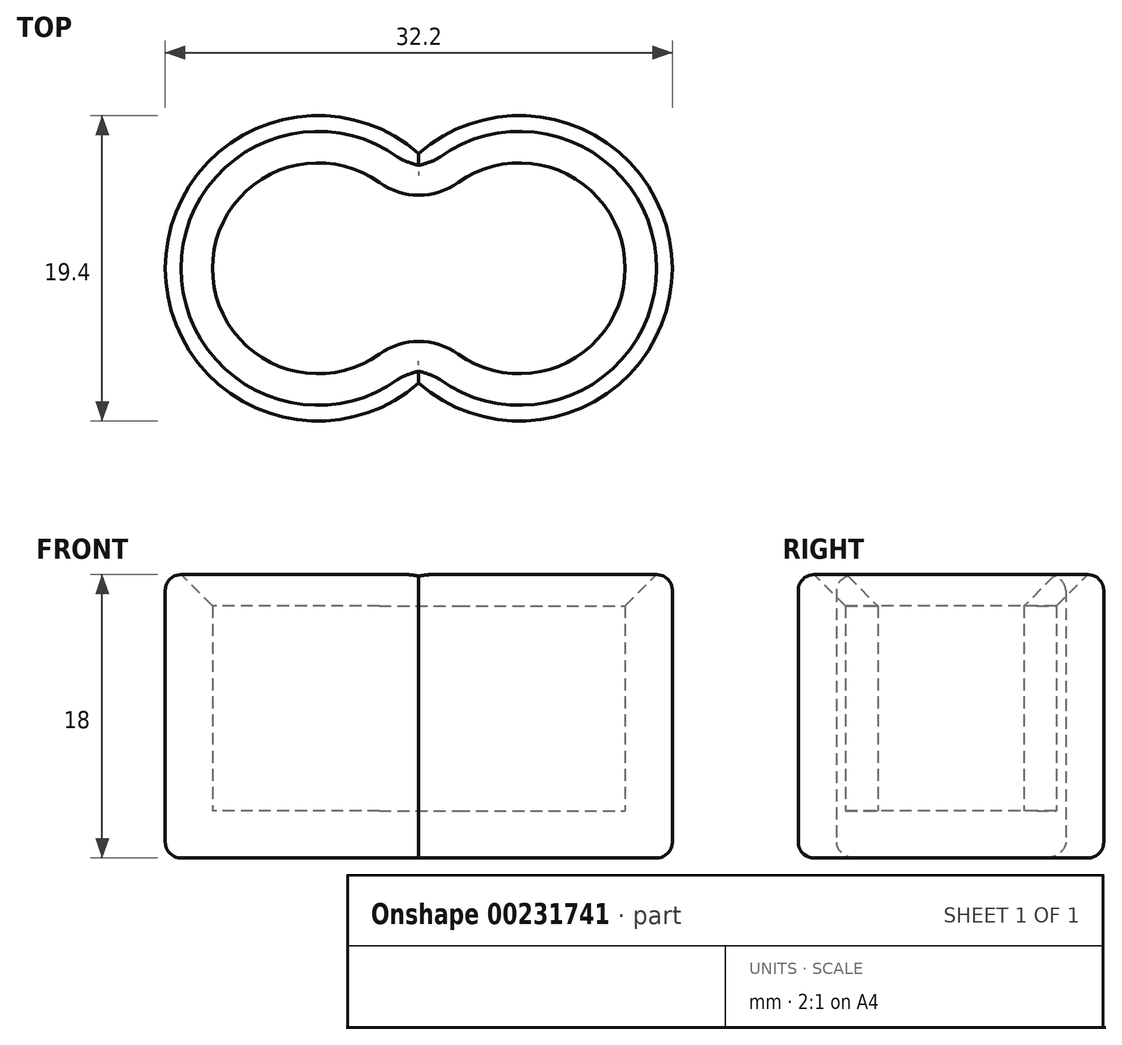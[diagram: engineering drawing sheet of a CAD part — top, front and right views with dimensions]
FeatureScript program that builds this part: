
annotation { "Feature Type Name" : "Feature", "Feature Type Description" : "" }
export const myFeature = defineFeature(function(context is Context, id is Id, definition is map)
    precondition{}
    {
        {
            var Q0;
            Q0=qCreatedBy(makeId("Top.planeOp"),FACE);
            var sketch = newSketch(context, id + "F0", { "sketchPlane" : qUnion([Q0])});
            skLineSegment(sketch, "E0", {"start": v(0, 0) * mm, "end": v(6.4, 0) * mm, "construction": true});
            skCircle(sketch, "E1", {"center": v(-6.4, 0) * mm, "radius": 6.7 * mm, "construction": true});
            skCircle(sketch, "E2", {"center": v(6.4, 0) * mm, "radius": 6.7 * mm, "construction": true});
            skArc(sketch, "E3.0", {"start": v(0, 7.29) * mm, "mid": v(-16.1, 0) * mm, "end": v(0, -7.29) * mm});
            skArc(sketch, "E4.0", {"start": v(0, -7.29) * mm, "mid": v(16.1, 0) * mm, "end": v(0, 7.29) * mm});
            skLineSegment(sketch, "E5.bottom", {"start": v(-2.5, 5.45) * mm, "end": v(2.5, 5.45) * mm, "construction": true});
            skLineSegment(sketch, "E5.top", {"start": v(-2.5, -5.45) * mm, "end": v(2.5, -5.45) * mm, "construction": true});
            skLineSegment(sketch, "E5.left", {"start": v(-2.5, 5.45) * mm, "end": v(-2.5, -5.45) * mm, "construction": true});
            skLineSegment(sketch, "E5.right", {"start": v(2.5, 5.45) * mm, "end": v(2.5, -5.45) * mm, "construction": true});
            skArc(sketch, "E6", {"start": v(-2.5, 5.45) * mm, "mid": v(0, 4.65) * mm, "end": v(2.5, 5.45) * mm});
            skArc(sketch, "E7", {"start": v(2.5, -5.45) * mm, "mid": v(0, -4.65) * mm, "end": v(-2.5, -5.45) * mm});
            skArc(sketch, "E8", {"start": v(-2.5, 5.45) * mm, "mid": v(-13.1, 0) * mm, "end": v(-2.5, -5.45) * mm});
            skArc(sketch, "E9", {"start": v(2.5, 5.45) * mm, "mid": v(13.1, 0) * mm, "end": v(2.5, -5.45) * mm});
            skSolve(sketch);
        }
        {
            var Q0;
            Q0=makeQuery(id+"F0.imprint","IMPRINT",FACE,{"disambiguationData":[TD([[makeQuery(id+"F0.imprint","IMPRINT",EDGE,{"derivedFrom":sQuery(id+"F0.wireOp",EDGE,"E3.0")}),1.0]])]});
            extrude(context, id + "F1", {"entities" : qUnion([Q0]), "depth" : 15 * mm});
        }
        {
            var Q0;
            Q0=makeQuery(id+"F1.opExtrude","CAP_FACE",FACE,{"disambiguationData":[OSD([sQuery(id+"F0.wireOp",EDGE,"E3.0"),sQuery(id+"F0.wireOp",EDGE,"E4.0"),sQuery(id+"F0.wireOp",EDGE,"E6"),sQuery(id+"F0.wireOp",EDGE,"E7"),sQuery(id+"F0.wireOp",EDGE,"E8"),sQuery(id+"F0.wireOp",EDGE,"E9")])],"isStart":true});
            var sketch = newSketch(context, id + "F2", { "sketchPlane" : qUnion([Q0])});
            skArc(sketch, "E10.0", {"start": v(0, 7.29) * mm, "mid": v(16.1, 0) * mm, "end": v(0, -7.29) * mm});
            skArc(sketch, "E11.0", {"start": v(0, -7.29) * mm, "mid": v(-16.1, 0) * mm, "end": v(0, 7.29) * mm});
            skSolve(sketch);
        }
        {
            var Q0;
            Q0 = qSketchRegion(id + "F2", true);
            extrude(context, id + "F3", {"entities" : qUnion([Q0]), "operationType" : NewBodyOperationType.ADD, "depth" : 3 * mm});
        }
        {
            var Q0;
            Q0=makeQuery(id+"F1.opExtrude","CAP_EDGE",EDGE,{"disambiguationData":[OSD([sQuery(id+"F0.wireOp",EDGE,"E8")])],"isStart":false});
            var Q1;
            Q1=makeQuery(id+"F1.opExtrude","CAP_EDGE",EDGE,{"disambiguationData":[OSD([sQuery(id+"F0.wireOp",EDGE,"E7")])],"isStart":false});
            var Q2;
            Q2=makeQuery(id+"F1.opExtrude","CAP_EDGE",EDGE,{"disambiguationData":[OSD([sQuery(id+"F0.wireOp",EDGE,"E6")])],"isStart":false});
            var Q3;
            Q3=makeQuery(id+"F1.opExtrude","CAP_EDGE",EDGE,{"disambiguationData":[OSD([sQuery(id+"F0.wireOp",EDGE,"E9")])],"isStart":false});
            chamfer(context, id + "F4", {"entities" : qUnion([Q0, Q1, Q2, Q3]), "width" : 2 * mm, "tangentPropagation" : true});
        }
        {
            var Q0;
            Q0=makeQuery(id+"F1.opExtrude","CAP_EDGE",EDGE,{"disambiguationData":[OSD([sQuery(id+"F0.wireOp",EDGE,"E3.0")])],"isStart":false});
            var Q1;
            Q1=makeQuery(id+"F1.opExtrude","CAP_EDGE",EDGE,{"disambiguationData":[OSD([sQuery(id+"F0.wireOp",EDGE,"E4.0")])],"isStart":false});
            var Q2;
            Q2=makeQuery(id+"F3.opExtrude","CAP_EDGE",EDGE,{"disambiguationData":[OSD([sQuery(id+"F2.wireOp",EDGE,"E11.0")])],"isStart":false});
            var Q3;
            Q3=makeQuery(id+"F3.opExtrude","CAP_EDGE",EDGE,{"disambiguationData":[OSD([sQuery(id+"F2.wireOp",EDGE,"E10.0")])],"isStart":false});
            fillet(context, id + "F5", {"entities" : qUnion([Q0, Q1, Q2, Q3]), "radius" : 1 * mm, "tangentPropagation" : true, "defaultsChanged" : true, "allowEdgeOverflow" : false, "vertexSettings" : [], "filletType" : FilletType.EDGE});
        }
    });
